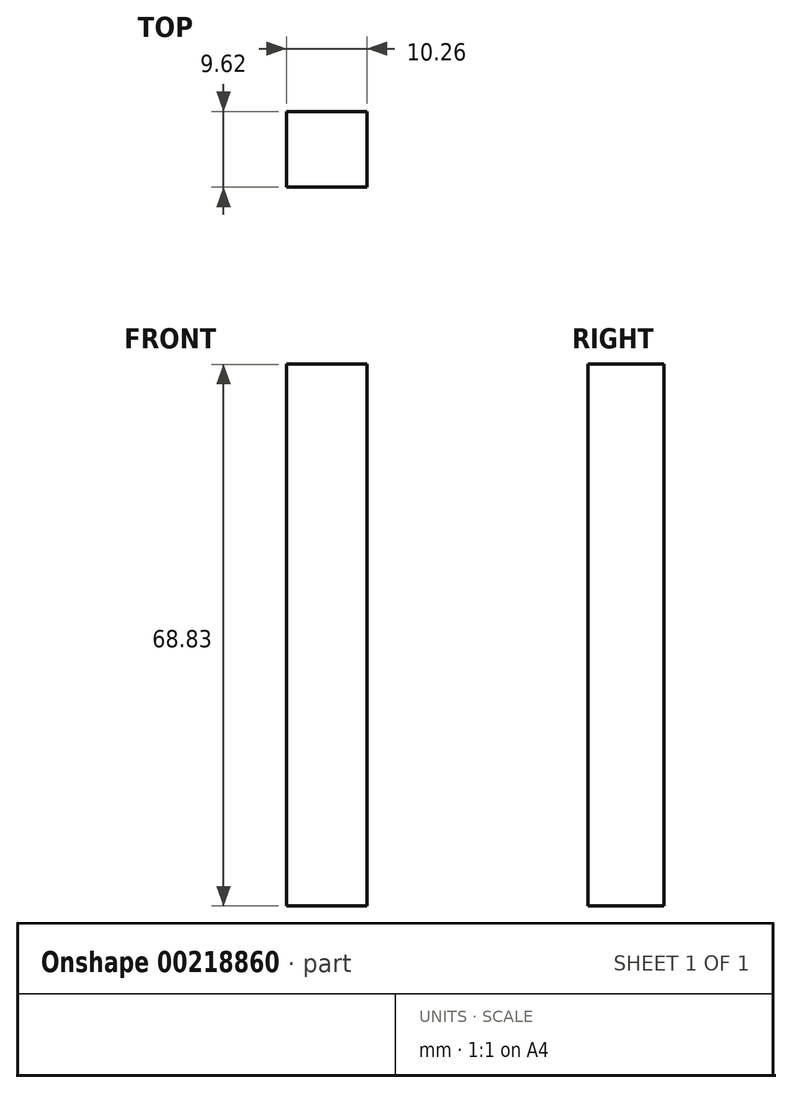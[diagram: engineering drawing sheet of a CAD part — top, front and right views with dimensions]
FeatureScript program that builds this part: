
annotation { "Feature Type Name" : "Feature", "Feature Type Description" : "" }
export const myFeature = defineFeature(function(context is Context, id is Id, definition is map)
    precondition{}
    {
        {
            var Q0;
            Q0=qCreatedBy(makeId("Top.planeOp"),FACE);
            var sketch = newSketch(context, id + "F0", { "sketchPlane" : qUnion([Q0])});
            skLineSegment(sketch, "E0.bottom", {"start": v(0, 0) * mm, "end": v(10.26, 0) * mm});
            skLineSegment(sketch, "E0.top", {"start": v(0, -9.62) * mm, "end": v(10.26, -9.62) * mm});
            skLineSegment(sketch, "E0.left", {"start": v(0, 0) * mm, "end": v(0, -9.62) * mm});
            skLineSegment(sketch, "E0.right", {"start": v(10.26, 0) * mm, "end": v(10.26, -9.62) * mm});
            skSolve(sketch);
        }
        {
            var Q0;
            Q0=makeQuery(id+"F0.imprint","IMPRINT",FACE,{"disambiguationData":[TD([[makeQuery(id+"F0.imprint","IMPRINT",EDGE,{"derivedFrom":sQuery(id+"F0.wireOp",EDGE,"E0.bottom")}),-1.0]])]});
            var sketch = newSketch(context, id + "F1", { "sketchPlane" : qUnion([Q0])});
            skSolve(sketch);
        }
        {
            var Q0;
            Q0 = qSketchRegion(id + "F1", true);
            var Q1;
            Q1=makeQuery(id+"F0.imprint","IMPRINT",FACE,{"disambiguationData":[TD([[makeQuery(id+"F0.imprint","IMPRINT",EDGE,{"derivedFrom":sQuery(id+"F0.wireOp",EDGE,"E0.bottom")}),-1.0]])]});
            extrude(context, id + "F2", {"entities" : qUnion([Q0, Q1]), "depth" : 68.83 * mm});
        }
    });
